# Revit family: EVO-Single
name_source: partatom
category: Lighting Fixtures
units: mm (PartAtom-declared; Revit-internal decimal feet)

## family parameters
Cut with Voids When Loaded = No
Host = Face
Light Source = No
OmniClass Number = 23.80.70.14.14
OmniClass Title = Exterior Floodlights
Part Type = Normal
Room Calculation Point = No
Round Connector Dimension = Use Diameter
Shared = No

## types (2) — shared parameters
Apparent Load = 3 VA
Default Elevation = 48.000"
Description = Outdoor LED Remote
Lamp = LED
Load Classification = Lighting
Manufacturer = Dual-lite
Model = EVO
Photometric Web = EVO Photometry : EVO
Tilt Angle = 10.00°
Total Input Wattage = 3 W
URL = https://www.currentlighting.com
Voltage = 120 V
Wattage Comments = 3
zz Angle1 = 10.00°

## per-type parameters (varying)
| type | Material Finish |
| EVO - Black | Paint - Black |
| EVO - White | Paint - White |

## geometry (parser evidence)
native form markers: Blend x11, Sweep x6
no freeform markers — native parametric forms only
